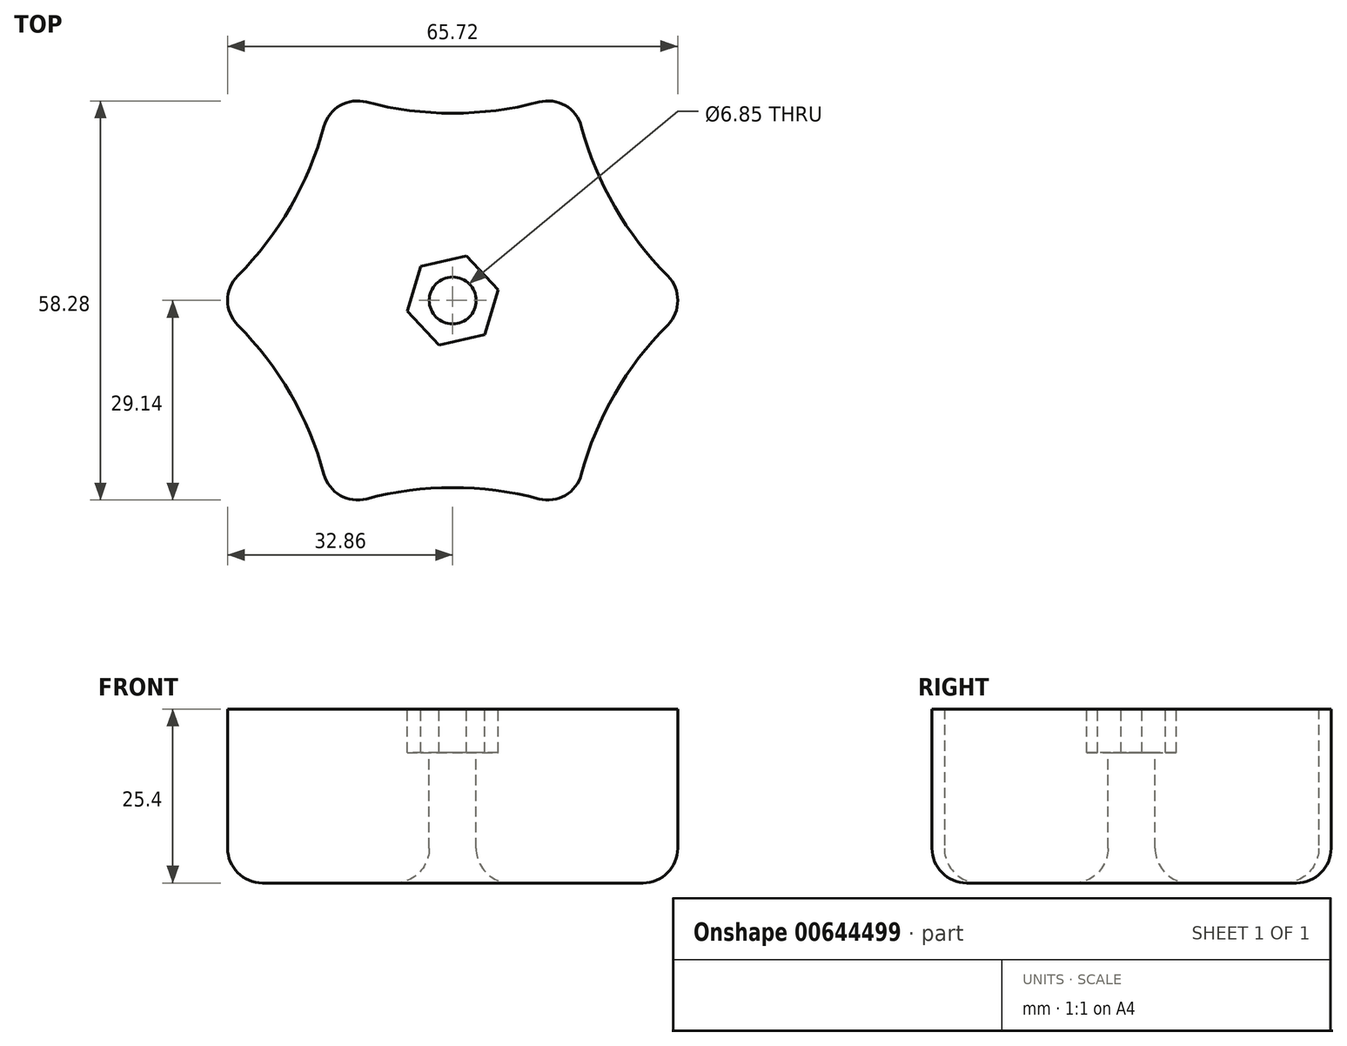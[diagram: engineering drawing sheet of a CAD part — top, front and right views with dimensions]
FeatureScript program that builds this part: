
annotation { "Feature Type Name" : "Feature", "Feature Type Description" : "" }
export const myFeature = defineFeature(function(context is Context, id is Id, definition is map)
    precondition{}
    {
        {
            var Q0;
            Q0=qCreatedBy(makeId("Top.planeOp"),FACE);
            var sketch = newSketch(context, id + "F0", { "sketchPlane" : qUnion([Q0])});
            skCircle(sketch, "E0.cCircle", {"center": v(0, 0) * mm, "radius": 30.62 * mm, "construction": true});
            skLineSegment(sketch, "E0.0", {"start": v(17.68, -30.62) * mm, "end": v(-17.68, -30.62) * mm});
            skLineSegment(sketch, "E0.1", {"start": v(-17.68, -30.62) * mm, "end": v(-35.36, 0) * mm});
            skLineSegment(sketch, "E0.2", {"start": v(-35.36, 0) * mm, "end": v(-17.68, 30.62) * mm});
            skLineSegment(sketch, "E0.3", {"start": v(-17.68, 30.62) * mm, "end": v(17.68, 30.62) * mm});
            skLineSegment(sketch, "E0.4", {"start": v(17.68, 30.62) * mm, "end": v(35.36, 0) * mm});
            skLineSegment(sketch, "E0.5", {"start": v(35.36, 0) * mm, "end": v(17.68, -30.62) * mm});
            skPoint(sketch, "E0.0.midPoint", {"position": v(0, -30.62) * mm});
            skArc(sketch, "E1", {"start": v(-35.36, 0) * mm, "mid": v(-23.66, 13.66) * mm, "end": v(-17.68, 30.62) * mm});
            skArc(sketch, "E2.1.0", {"start": v(-17.68, -30.62) * mm, "mid": v(-23.66, -13.66) * mm, "end": v(-35.36, 0) * mm});
            skArc(sketch, "E2.2.0", {"start": v(17.68, -30.62) * mm, "mid": v(0, -27.33) * mm, "end": v(-17.68, -30.62) * mm});
            skArc(sketch, "E2.3.0", {"start": v(35.36, 0) * mm, "mid": v(23.66, -13.66) * mm, "end": v(17.68, -30.62) * mm});
            skArc(sketch, "E2.4.0", {"start": v(17.68, 30.62) * mm, "mid": v(23.66, 13.66) * mm, "end": v(35.36, 0) * mm});
            skArc(sketch, "E2.5.0", {"start": v(-17.68, 30.62) * mm, "mid": v(0, 27.33) * mm, "end": v(17.68, 30.62) * mm});
            skSolve(sketch);
        }
        {
            var Q0;
            Q0=makeQuery(id+"F0.imprint","IMPRINT",FACE,{"disambiguationData":[TD([[makeQuery(id+"F0.imprint","IMPRINT",EDGE,{"derivedFrom":sQuery(id+"F0.wireOp",EDGE,"E1")}),-1.0]])]});
            extrude(context, id + "F1", {"entities" : qUnion([Q0]), "depth" : 25.4 * mm, "offsetDistance" : 25.4 * mm});
        }
        {
            var Q0;
            Q0=makeQuery(id+"F1.opExtrude","CAP_FACE",FACE,{"disambiguationData":[OSD([sQuery(id+"F0.wireOp",EDGE,"E1"),sQuery(id+"F0.wireOp",EDGE,"E2.1.0"),sQuery(id+"F0.wireOp",EDGE,"E2.2.0"),sQuery(id+"F0.wireOp",EDGE,"E2.3.0"),sQuery(id+"F0.wireOp",EDGE,"E2.4.0"),sQuery(id+"F0.wireOp",EDGE,"E2.5.0")])],"isStart":false});
            var sketch = newSketch(context, id + "F2", { "sketchPlane" : qUnion([Q0])});
            skCircle(sketch, "E3", {"center": v(0, 0) * mm, "radius": 3.43 * mm});
            skSolve(sketch);
        }
        {
            var Q0;
            Q0 = qSketchRegion(id + "F2", true);
            extrude(context, id + "F3", {"entities" : qUnion([Q0]), "operationType" : NewBodyOperationType.REMOVE, "oppositeDirection" : true, "depth" : 25.4 * mm, "offsetDistance" : 25.4 * mm});
        }
        {
            var Q0;
            Q0=makeQuery(id+"F1.opExtrude","SWEPT_EDGE",EDGE,{"disambiguationData":[OSD([sQuery(id+"F0.wireOp",EDGE,"E0.1"),sQuery(id+"F0.wireOp",EDGE,"E0.2"),sQuery(id+"F0.wireOp",EDGE,"E1"),sQuery(id+"F0.wireOp",EDGE,"E2.1.0")])]});
            var Q1;
            Q1=makeQuery(id+"F1.opExtrude","SWEPT_EDGE",EDGE,{"disambiguationData":[OSD([sQuery(id+"F0.wireOp",EDGE,"E0.0"),sQuery(id+"F0.wireOp",EDGE,"E0.1"),sQuery(id+"F0.wireOp",EDGE,"E2.1.0"),sQuery(id+"F0.wireOp",EDGE,"E2.2.0")])]});
            var Q2;
            Q2=makeQuery(id+"F1.opExtrude","SWEPT_EDGE",EDGE,{"disambiguationData":[OSD([sQuery(id+"F0.wireOp",EDGE,"E0.0"),sQuery(id+"F0.wireOp",EDGE,"E0.5"),sQuery(id+"F0.wireOp",EDGE,"E2.2.0"),sQuery(id+"F0.wireOp",EDGE,"E2.3.0")])]});
            var Q3;
            Q3=makeQuery(id+"F1.opExtrude","SWEPT_EDGE",EDGE,{"disambiguationData":[OSD([sQuery(id+"F0.wireOp",EDGE,"E0.4"),sQuery(id+"F0.wireOp",EDGE,"E0.5"),sQuery(id+"F0.wireOp",EDGE,"E2.3.0"),sQuery(id+"F0.wireOp",EDGE,"E2.4.0")])]});
            var Q4;
            Q4=makeQuery(id+"F1.opExtrude","SWEPT_EDGE",EDGE,{"disambiguationData":[OSD([sQuery(id+"F0.wireOp",EDGE,"E0.3"),sQuery(id+"F0.wireOp",EDGE,"E0.4"),sQuery(id+"F0.wireOp",EDGE,"E2.4.0"),sQuery(id+"F0.wireOp",EDGE,"E2.5.0")])]});
            var Q5;
            Q5=makeQuery(id+"F1.opExtrude","SWEPT_EDGE",EDGE,{"disambiguationData":[OSD([sQuery(id+"F0.wireOp",EDGE,"E0.2"),sQuery(id+"F0.wireOp",EDGE,"E0.3"),sQuery(id+"F0.wireOp",EDGE,"E1"),sQuery(id+"F0.wireOp",EDGE,"E2.5.0")])]});
            var Q6;
            Q6=makeQuery(id+"F1.opExtrude","CAP_FACE",FACE,{"disambiguationData":[OSD([sQuery(id+"F0.wireOp",EDGE,"E1"),sQuery(id+"F0.wireOp",EDGE,"E2.1.0"),sQuery(id+"F0.wireOp",EDGE,"E2.2.0"),sQuery(id+"F0.wireOp",EDGE,"E2.3.0"),sQuery(id+"F0.wireOp",EDGE,"E2.4.0"),sQuery(id+"F0.wireOp",EDGE,"E2.5.0")])],"isStart":true});
            fillet(context, id + "F4", {"entities" : qUnion([Q0, Q1, Q2, Q3, Q4, Q5, Q6]), "radius" : 5.08 * mm, "tangentPropagation" : true, "allowEdgeOverflow" : false});
        }
        {
            var Q0;
            Q0=makeQuery(id+"F1.opExtrude","CAP_FACE",FACE,{"disambiguationData":[OSD([sQuery(id+"F0.wireOp",EDGE,"E1"),sQuery(id+"F0.wireOp",EDGE,"E2.1.0"),sQuery(id+"F0.wireOp",EDGE,"E2.2.0"),sQuery(id+"F0.wireOp",EDGE,"E2.3.0"),sQuery(id+"F0.wireOp",EDGE,"E2.4.0"),sQuery(id+"F0.wireOp",EDGE,"E2.5.0")])],"isStart":false});
            var sketch = newSketch(context, id + "F5", { "sketchPlane" : qUnion([Q0])});
            skCircle(sketch, "E4.cCircle", {"center": v(0, 0) * mm, "radius": 5.9 * mm, "construction": true});
            skLineSegment(sketch, "E4.0", {"start": v(4.65, -4.98) * mm, "end": v(-1.99, -6.52) * mm});
            skLineSegment(sketch, "E4.1", {"start": v(-1.99, -6.52) * mm, "end": v(-6.64, -1.54) * mm});
            skLineSegment(sketch, "E4.2", {"start": v(-6.64, -1.54) * mm, "end": v(-4.65, 4.98) * mm});
            skLineSegment(sketch, "E4.3", {"start": v(-4.65, 4.98) * mm, "end": v(1.99, 6.52) * mm});
            skLineSegment(sketch, "E4.4", {"start": v(1.99, 6.52) * mm, "end": v(6.64, 1.54) * mm});
            skLineSegment(sketch, "E4.5", {"start": v(6.64, 1.54) * mm, "end": v(4.65, -4.98) * mm});
            skPoint(sketch, "E4.0.midPoint", {"position": v(1.33, -5.75) * mm});
            skSolve(sketch);
        }
        {
            var Q0;
            Q0 = qSketchRegion(id + "F5", true);
            extrude(context, id + "F6", {"entities" : qUnion([Q0]), "operationType" : NewBodyOperationType.REMOVE, "oppositeDirection" : true, "depth" : 6.35 * mm, "offsetDistance" : 25.4 * mm});
        }
    });
